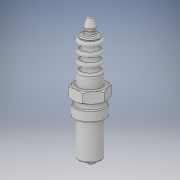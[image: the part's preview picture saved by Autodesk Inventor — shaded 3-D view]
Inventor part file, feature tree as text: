
AUTODESK INVENTOR PART (.ipt)
format: ipt  version: 2018 (Build 220112000, 112)  size: 442,368 bytes
history: native  units: mm
features: sketch x9, extrude x4, revolve x3, fillet x2, projected_geometry x2, plane x1, sweep x1
ambient origin geometry x8: Origin, YZ Plane, XZ Plane, XY Plane, X Axis, Y Axis, Z Axis, Center Point
bodies: Solid1 (feature_tree), Solid2 (feature_tree), Solid3 (feature_tree)
feature tree (22):
  revolve  "Revolution1"  [1 undecoded]
  revolve  "Revolution2"  [1 undecoded]
  plane  "Work Plane1"
  extrude  "Extrusion1"  Depth=0.25mm
  revolve  "Revolution3"  [1 undecoded]
  extrude  "Extrusion2"  Depth=2.0mm
  extrude  "Extrusion3"  TaperAngle=90.0deg  [1 undecoded]
  extrude  "Extrusion4"  Depth=0.25mm
  sweep  "Sweep1"
  fillet  "Fillet1"  Radius=0.9mm
  fillet  "Fillet2"  Radius=11.419689mm
  sketch  "Sketch1"  dims[d0=17.5mm d1=2.0mm]
  sketch  "Sketch2"  dims[d2=1.0mm d3=60.0mm d5=1.0mm d6=10.0mm d8=10.0mm]
  sketch  "Sketch3"  dims[d10=20.0mm d12=1.0mm d13=10.0mm d15=10.0mm d17=0.25mm]
  sketch  "Sketch4"  dims[d18=0.25mm d19=1.75mm]
  sketch  "Sketch5"  dims[d20=0.04mm d21=2.0mm]
  sketch  "Sketch6"  dims[d22=7.0mm d23=90.0deg]
  sketch  "Sketch7"  dims[d24=0.083mm d25=0.25mm]
  sketch  "Sketch8"  dims[d26=2.125mm d27=3.42mm d28=0.9mm d29=11.419689mm]
  projected_geometry  "Projected Loop1"
  sketch  "Sketch9"  dims[d30=3.413864mm d31=2.01mm d32=0.25mm d33=0.620228mm d34=90.0deg d35=-14.0mm d36=3.9mm d37=2.4mm d38=0.0mm d39=11.0mm d40=1.2mm d41=3.35mm d43=0.25mm d44=90.0deg d45=4100.0mm d46=0.0mm d47=100.0mm d48=60.0deg d49=25.0mm d50=50.0mm d51=60.0deg d52=0.0mm d53=0.5mm d54=1.4mm d55=1.0mm d56=0.0mm d57=1.0mm d58=3.0mm d59=8.0mm d60=8.0mm d61=0.0mm d62=0.0mm d63=0.15mm d64=0.25mm]
  projected_geometry  "Project Cut Edges1"
note: 4 required parameter values undecoded (feature->parameter linkage not recoverable at this tier; creation-order binding heuristic only, values carry confidence <= 0.55)